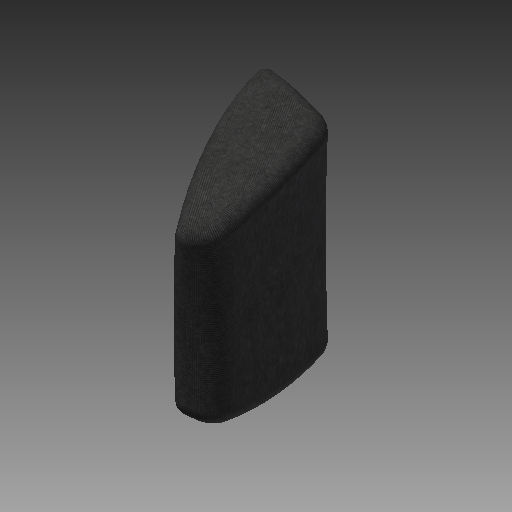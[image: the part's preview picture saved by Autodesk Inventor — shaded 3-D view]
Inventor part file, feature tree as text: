
AUTODESK INVENTOR PART (.ipt)
format: ipt  version: 2019 (Build 230136000, 136)  size: 2,392,064 bytes
history: native  units: mm
features: surface_op x34, sketch x14, other x9, fillet x8, sweep x5, plane x4, extrude x2, mirror x1, shell x1
ambient origin geometry x8: Origin, YZ Plane, XZ Plane, XY Plane, X Axis, Y Axis, Z Axis, Center Point
bodies: Solid1 (feature_tree)
feature tree (78):
  sketch  "Sketch1"  dims[d15=20.0mm d16=62.0mm d17=62.0mm d18=20.0mm d19=104.0mm d20=170.0mm]
  sketch  "Sketch2"  dims[d21=104.0mm d22=170.0mm]
  sketch  "Sketch3"  dims[d23=614.0mm d24=0.069mm]
  sketch  "Sketch5"  dims[d27=0.387465mm d28=2.298794mm]
  sketch  "Sketch6"  dims[d29=2.298794mm d30=16.0mm]
  sketch  "Sketch7"  dims[d31=16.0mm d32=0.0mm]
  sketch  "Sketch9"  dims[d33=29.0mm]
  plane  "Work Plane1"
  sketch  "Sketch10"  dims[d34=29.0mm]
  plane  "Work Plane2"
  sketch  "Sketch11"  dims[d35=72.0mm]
  sketch  "Sketch13"  dims[d37=111.5mm]
  plane  "Work Plane4"
  mirror  "Mirror1"
  surface_op  "Trim5"
  surface_op  "Extend1"
  surface_op  "Extend2"
  surface_op  "Trim7"
  surface_op  "Trim8"
  surface_op  "Trim9"
  surface_op  "Trim10"
  surface_op  "Trim11"
  surface_op  "Trim12"
  surface_op  "Trim13"
  surface_op  "Trim14"
  surface_op  "Extend3"
  surface_op  "Extend6"
  surface_op  "Extend7"
  surface_op  "Trim16"
  surface_op  "Trim17"
  surface_op  "Trim18"
  surface_op  "Extend4"
  surface_op  "Extend5"
  surface_op  "Trim19"
  surface_op  "Trim20"
  surface_op  "Trim21"
  surface_op  "Trim22"
  surface_op  "Trim26"
  surface_op  "Stitch Surface2"
  surface_op  "Trim27"
  surface_op  "Trim28"
  fillet  "Fillet6"  Radius=2.225295mm
  fillet  "Fillet7"  Radius=300.0mm
  fillet  "Fillet8"  [1 undecoded]
  fillet  "Fillet9"  [1 undecoded]
  surface_op  "Extend8"
  surface_op  "Extend9"
  surface_op  "Trim29"
  surface_op  "Trim30"
  surface_op  "Stitch Surface3"
  fillet  "Fillet10"  [1 undecoded]
  extrude  "Extrusion1"  Depth=62.0mm
  fillet  "Fillet12"  Radius=62.0mm
  fillet  "Fillet13"  Radius=20.0mm
  fillet  "Fillet14"  Radius=104.0mm
  shell  "Shell1"  Thickness=170.0mm
  sketch  "Sketch4"  dims[d25=0.387465mm d26=0.069mm]
  other  "Srf1"
  other  "Srf2"
  sketch  "Sketch12"  dims[d36=72.0mm]
  other  "Srf3"
  plane  "Work Plane3"
  other  "Srf4"
  sketch  "Sketch16"  dims[d38=111.5mm]
  other  "Srf5"
  other  "Srf6"
  other  "Srf8"
  sketch  "Sketch17"  dims[d39=162.0mm d40=162.0mm d41=2.0mm d42=2.0mm d43=10.5mm d44=10.5mm d45=26.0mm d46=26.0mm d47=70.0mm d48=70.0mm d49=718.25mm d50=-427.0mm d51=-232.75mm d100=0.0mm d101=192.25mm d102=52.0mm d103=92.0mm d104=134.25mm d105=170.0mm d106=52.0mm d107=92.0mm d108=134.25mm d109=170.0mm d110=0.5mm d111=3.0mm d112=8.7mm d113=18.3mm d114=0.5mm d115=3.0mm d116=8.7mm d117=18.3mm d118=0.0mm d119=30.0mm d120=30.0mm d121=19.0mm d122=45.0mm d123=45.0mm d124=23.5mm d125=23.5mm d156=30.0mm d157=15.0mm d158=35.0mm d159=10.0mm d160=18.25mm d161=19.0mm d162=15.0mm d163=93.0mm d164=46.0mm d165=192.0mm d167=96.0mm d168=25.0mm d169=13.0mm d170=13.0mm d171=5.0mm d172=0.0mm d174=5.0mm d175=1.0mm d176=5.0mm d177=5.0mm d178=0.254mm d179=0.254mm d180=0.0mm d181=0.0mm d182=0.0mm d183=0.0mm]
  extrude  "ExtrusionSrf1"  Depth=170.0mm
  sweep  "SweepSrf4"
  sweep  "SweepSrf5"
  sweep  "SweepSrf6"
  sweep  "SweepSrf7"
  surface_op  "Surface2"
  surface_op  "Surface3"
  sweep  "SweepSrf8"
  other  "Srf7"
  other  "Srf9"
note: 3 required parameter values undecoded (feature->parameter linkage not recoverable at this tier; creation-order binding heuristic only, values carry confidence <= 0.55)
